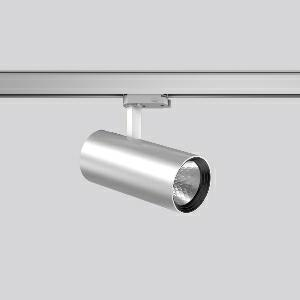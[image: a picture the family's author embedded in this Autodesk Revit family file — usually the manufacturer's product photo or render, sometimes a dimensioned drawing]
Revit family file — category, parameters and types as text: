
# Revit family: deecos_s_mini_742195_004_2_13bc
name_source: partatom
category: Lighting Fixtures
units: mm (PartAtom-declared; Revit-internal decimal feet)

## family parameters
Cut with Voids When Loaded = No
Host = Face
Light Source = No
Part Type = Normal
Room Calculation Point = No
Round Connector Dimension = Use Diameter
Shared = No

## types (1)
- DEECOS S mini (1 x LED Modul 927, 2400 lm, 2700)
    Apparent Load = 20 VA
    Approval mark = CE
    CIE Flux Codes = 100 100 100 100 100
    Color Rendering = 92
    Color Temperature = 2700
    Default Elevation = 1800 mm
    Description = Series: DEECOS S mini
LED surface-mounted projector in modern design with no visible cooling ribs. Housing: die-cast aluminium, powder-coated. Rotation range: 356°. Swivel range: 90°. Black plastic ring and recessed LED to prevent glare from the side. Optical assembly with reflector made of MIRO-Silver with 98% total light reflection for outstanding efficiency - can be changed without tools. Best colour rendering index Ra>90. With multi adaptor for 3-circuit tracks 230 V. Suitable for Track on ceiling, Wall track. High quality converter without flickering and stroboscopic effect. The following accessories can be mounted without use of tools: interchangeable lenses, decorative glasses, honeycomb louvre, clear and frosted diffusers, white interchangeable plastic ring. 
Colour: silver
Diameter: 87 mm
Height: 214 mm
Lamp: LED
Socket: without socket
Colour temperature: 2700K
Colour rendering index (CRI): 92
System power: 20 W
Rated luminous flux: 2400 lm
Luminous efficiency: 120 lm/W
Control gear: Regulated power supply
Protection class: I
Type of protection: IP 20
    Height = 214 mm
    Lamp = 1 x LED Modul 927
    Lamp Light Flux = 2400 lm
    Lamp count = 1
    Length = 87 mm
    Lifetime = 50000 h
    Luminous efficacy = 120 lm/W
    Manufacturer = RZB
    ModVariant = No
    Model = 742195.004.2
    Mounting Place = Ceiling
    Mounting Type = Rail mounted
    Number of Poles = 1
    OnlyDefault = Yes
    Power Factor = 1
    Product Name = DEECOS S mini
    Product group = Track mounted projectors
    ProductGroupID = 301
    Protection Class = Protection class I
    Protection Degree = IP 20
    RLX_Detail_Level = 1
    RLX_Emergency_Light_Flux = 0 lm
    RLX_Emergency_Type = 0
    RLX_Emergency_Type_DB = No
    RlxData = <blob elided: 37117 chars, md5=49112e4e>
    Socket = socket
    Standby Power = 0 W
    System Light Flux = 2400 lm
    System Power = 20 W
    Type Comments = Product without accessories
    Type Image = 741926.004.jpg
    URL = http://relux.com
    VarID = ---
    Voltage = 230 V
    Voltage Range = 220-240 V
    Weight = 0.00 kg
    Width = 0 mm  [stored 0 ft]

note: [stored X ft] marks values corroborated as IEEE doubles in the binary element streams (Revit-internal decimal feet)

## geometry (parser evidence)
native form markers: Blend x4, Sweep x14
no freeform markers — native parametric forms only
